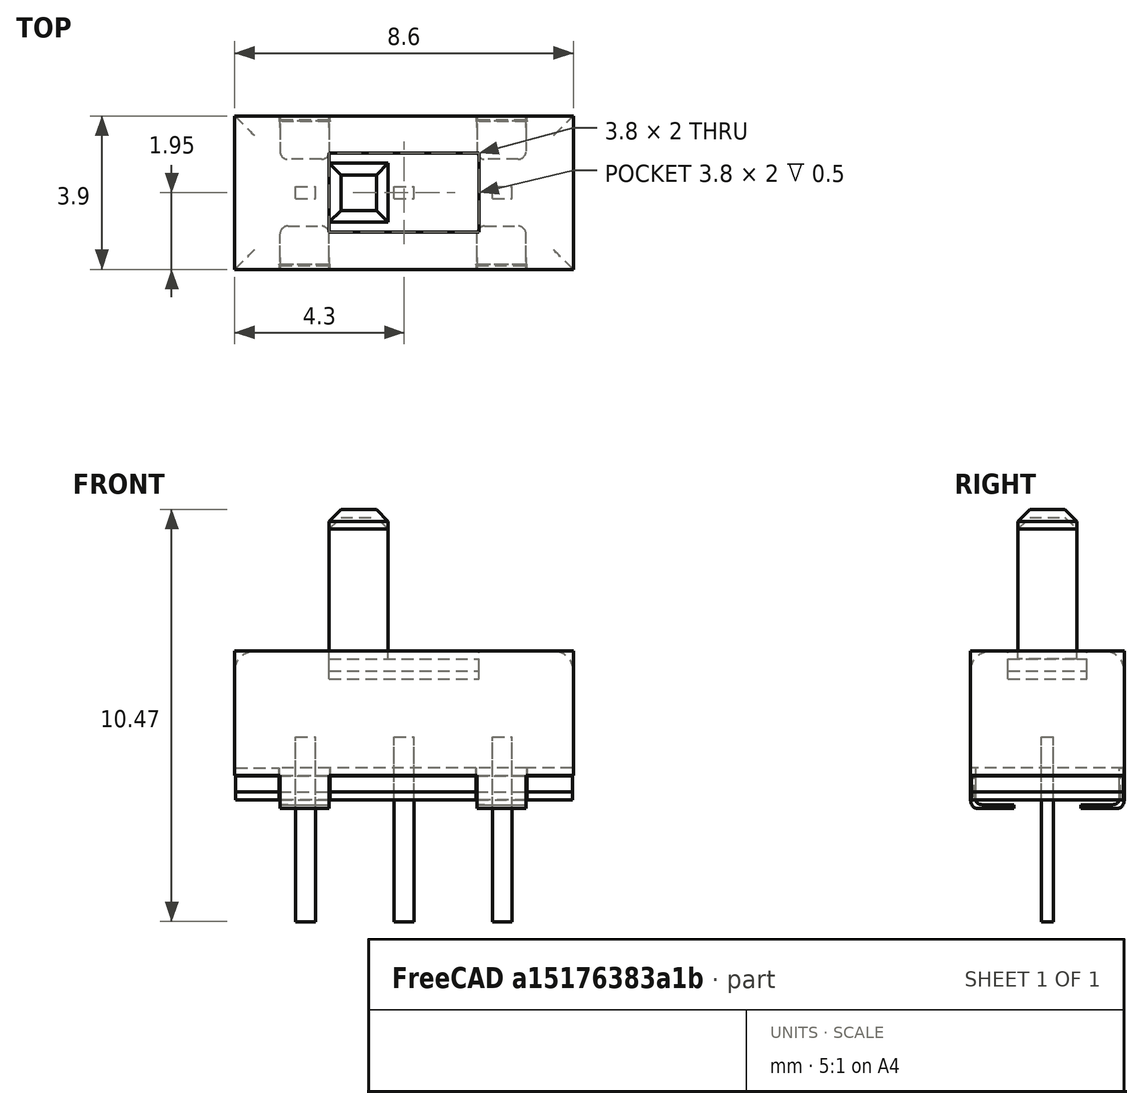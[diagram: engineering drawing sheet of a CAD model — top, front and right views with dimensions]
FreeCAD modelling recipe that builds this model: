
FCSTD DOCUMENT  (FreeCAD 0.18R16131 (Git))
Label: interruptor conmuntador PCB
License: Public Domain
LicenseURL: http://en.wikipedia.org/wiki/Public_domain
objects: Part::Box×14, Part::MultiFuse×6, Part::Feature×6, Part::Fillet×5, Part::Part2DObjectPython×2, Part::Cut×2, Part::Offset×1, Part::Chamfer×1, Part::FeaturePython×1, App::DocumentObjectGroup×1
note: 38 computed .brp shape members not serialized (recipe doc carries the construction recipe); baked Part::Feature solids carry a one-line shape summary decoded from their .brp

FEATURE [Part::Box] Box  label="Chapa"
  AttacherType = Attacher::AttachEngine3D
  Height = 3.15
  Length = 8.6
  Placement = pos=(0,0,0.75) rot=(0,0,1;0rad)
  Width = 3.9
FEATURE [Part::Box] Box001  label="cubo fibra"
  AttacherType = Attacher::AttachEngine3D
  Height = 0.75
  Length = 8.6
  Placement = pos=(0,0,0.1) rot=(0,0,1;0rad)
  Width = 3.9
FEATURE [Part::Box] Box002  label="Cubo"
  AttacherType = Attacher::AttachEngine3D
  Height = 0.1
  Length = 1.25
  Placement = pos=(2.15,0,-0.1) rot=(0,0,1;0rad)
  Width = 1.1
FEATURE [Part::Box] Box003  label="Cubo001"
  AttacherType = Attacher::AttachEngine3D
  Height = 0.75
  Length = 1.25
  Placement = pos=(2.15,0,0) rot=(0,0,1;0rad)
  Width = 0.1
FEATURE [Part::MultiFuse] Fusion
  Refine = true
  Shapes = -> [Box002,Box003]
FEATURE [Part::Fillet] Fillet  label="pata"
  Base = -> Fusion
  Edges = 4 edges r=0.2: [Edge4,Edge6,Edge7,Edge10]
  Placement = pos=(-1,0,0) rot=(0,0,1;0rad)
FEATURE [Part::Box] Box004  label="Cubo002"
  AttacherType = Attacher::AttachEngine3D
  Height = 0.1
  Length = 1.25
  Placement = pos=(2.15,0,-0.1) rot=(0,0,1;0rad)
  Width = 1.1
FEATURE [Part::Box] Box005  label="Cubo003"
  AttacherType = Attacher::AttachEngine3D
  Height = 0.75
  Length = 1.25
  Placement = pos=(2.15,0,0) rot=(0,0,1;0rad)
  Width = 0.1
FEATURE [Part::MultiFuse] Fusion001
  Refine = true
  Shapes = -> [Box004,Box005]
FEATURE [Part::Fillet] Fillet001  label="pata001"
  Base = -> Fusion001
  Edges = 4 edges r=0.2: [Edge4,Edge6,Edge7,Edge10]
  Placement = pos=(4,0,0) rot=(0,0,1;0rad)
FEATURE [Part::Box] Box006  label="Cubo004"
  AttacherType = Attacher::AttachEngine3D
  Height = 0.1
  Length = 1.25
  Placement = pos=(2.15,0,-0.1) rot=(0,0,1;0rad)
  Width = 1.1
FEATURE [Part::Box] Box007  label="Cubo005"
  AttacherType = Attacher::AttachEngine3D
  Height = 0.75
  Length = 1.25
  Placement = pos=(2.15,0,0) rot=(0,0,1;0rad)
  Width = 0.1
FEATURE [Part::MultiFuse] Fusion002
  Refine = true
  Shapes = -> [Box006,Box007]
FEATURE [Part::Fillet] Fillet002  label="pata002"
  Base = -> Fusion002
  Edges = 4 edges r=0.2: [Edge4,Edge6,Edge7,Edge10]
  Placement = pos=(4.55,3.9,0) rot=(0,0,1;3.14159rad)
FEATURE [Part::Box] Box008  label="Cubo006"
  AttacherType = Attacher::AttachEngine3D
  Height = 0.1
  Length = 1.25
  Placement = pos=(2.15,0,-0.1) rot=(0,0,1;0rad)
  Width = 1.1
FEATURE [Part::Box] Box009  label="Cubo007"
  AttacherType = Attacher::AttachEngine3D
  Height = 0.75
  Length = 1.25
  Placement = pos=(2.15,0,0) rot=(0,0,1;0rad)
  Width = 0.1
FEATURE [Part::MultiFuse] Fusion003
  Refine = true
  Shapes = -> [Box008,Box009]
FEATURE [Part::Fillet] Fillet003  label="pata003"
  Base = -> Fusion003
  Edges = 4 edges r=0.2: [Edge4,Edge6,Edge7,Edge10]
  Placement = pos=(9.55,3.9,0) rot=(0,0,1;3.14159rad)
FEATURE [Part::Part2DObjectPython] Line  # Draft 2D object (typed FeaturePython)
  ChamferSize = 0
  Closed = false
  End = (7.4,3.9,0.75)
  FilletRadius = 0
  Length = 3.9
  MakeFace = true
  Placement = pos=(7.4,0,0.75) rot=(0.707107,-0.707107,0;3.14159rad)
  Points = (2) [(0,0,0),(-3.9,-8.88178e-16,0)]
  Start = (7.4,0,0.75)
  Subdivisions = 0
  Support = -> [Box]
FEATURE [Part::Part2DObjectPython] Line001  # Draft 2D object (typed FeaturePython)
  ChamferSize = 0
  Closed = false
  End = (2.4,3.9,0.75)
  FilletRadius = 0
  Length = 3.8904
  MakeFace = true
  Placement = pos=(2.4,0.00960443,0.745004) rot=(0.57735,0.57735,0.57735;2.0944rad)
  Points = (2) [(0,0,0),(3.8904,0.00499602,0)]
  Start = (2.4,0.00960443,0.745004)
  Subdivisions = 0
FEATURE [Part::MultiFuse] Fusion004  label="Cuerpo metalico"
  Placement = pos=(0,0,-0.2) rot=(0,0,1;0rad)
  Refine = true
  Shapes = -> [Fillet003,Fillet002,Fillet001,Fillet,Box]
FEATURE [Part::Feature] Fusion004001  label="Fusion005"
  shape: bbox 8.6 x 3.9 x 4 mm, 46 faces (baked)
FEATURE [Part::Cut] Cut  label="Fibra src"
  Base = -> Box001
  Refine = true
  Tool = -> Fusion004001
FEATURE [Part::Offset] Offset  label="Offset fibra"
  Fill = false
  Intersection = true
  Join = 2
  Mode = 0
  SelfIntersection = false
  Source = -> Cut
  Value = -0.02
FEATURE [Part::Feature] Offset001  label="Fibra"
  Placement = pos=(0,0,-0.2) rot=(0,0,1;0rad)
  shape: bbox 8.562 x 3.862 x 0.612 mm, 26 faces (baked)
FEATURE [Part::Box] Box010  label="Cubo008"
  AttacherType = Attacher::AttachEngine3D
  Height = 0.5
  Length = 3.8
  Placement = pos=(2.4,0.95,3.2) rot=(0,0,1;0rad)
  Width = 2
FEATURE [Part::Cut] Cut001  label="src cuerpo metalico"
  Base = -> Fusion004
  Refine = true
  Tool = -> Box010
FEATURE [Part::Box] Box011  label="Cubo interruptor"
  AttacherType = Attacher::AttachEngine3D
  Height = 3.7
  Length = 1.5
  Placement = pos=(2.4,1.2,3.6) rot=(0,0,1;0rad)
  Width = 1.5
FEATURE [Part::Box] Box012  label="Cubo009"
  AttacherType = Attacher::AttachEngine3D
  Height = 0.5
  Length = 3.8
  Placement = pos=(2.4,0.95,3.2) rot=(0,0,1;0rad)
  Width = 2
FEATURE [Part::MultiFuse] Fusion004002  label="src fusion palito interruptor"
  Refine = true
  Shapes = -> [Box011,Box012]
FEATURE [Part::Chamfer] Chamfer  label="src chaflan interruptor"
  Base = -> Fusion004002
  Edges = 4 edges r=0.3: [Edge18,Edge20,Edge21,Edge22]
FEATURE [Part::Feature] Chamfer001  label="Interuptor"
  Placement = pos=(0,0,-0.2) rot=(0,0,1;0rad)
  shape: bbox 3.8 x 2 x 4.1 mm, 14 faces (baked)
FEATURE [Part::Feature] Cut001001  label="cuerpo metalico"
  shape: bbox 8.6 x 3.9 x 4 mm, 51 faces (baked)
FEATURE [Part::Box] Box013  label="Cubo010"
  AttacherType = Attacher::AttachEngine3D
  Height = 4.7
  Length = 0.5
  Placement = pos=(0,0,4.7) rot=(0,0,1;0rad)
  Width = 0.3
FEATURE [Part::FeaturePython] Array  label="src pines"  # Draft array (typed FeaturePython)
  Angle = 360
  ArrayType = 0
  Axis = (0,0,1)
  Base = -> Box013
  Center = (0,0,0)
  Fuse = false
  IntervalAxis = (0,0,0)
  IntervalX = (2.5,0,0)
  IntervalY = (0,1,0)
  IntervalZ = (0,0,1)
  NumberPolar = 1
  NumberX = 3
  NumberY = 1
  NumberZ = 1
  Placement = pos=(1.55047,1.8,-7.875) rot=(0,0,1;0rad)
FEATURE [Part::Feature] Array001  label="pines"
  Placement = pos=(1.55047,1.8,-7.875) rot=(0,0,1;0rad)
  shape: bbox 5.5 x 0.3 x 4.7 mm, 18 faces, 3 solids (baked)
FEATURE [Part::Fillet] Fillet004
  Base = -> Cut001001
  Edges = 4 edges r=0.5: [Edge2,Edge15,Edge16,Edge17]
FEATURE [App::DocumentObjectGroup] Group  label="src"
  Group = -> [Cut,Offset,Cut001,Line,Line001,Fusion004002,Chamfer,Array,Fillet004]
FEATURE [Part::Feature] Fillet004001  label="cuerpo"
  shape: bbox 8.6 x 3.9 x 4 mm, 55 faces (baked)
